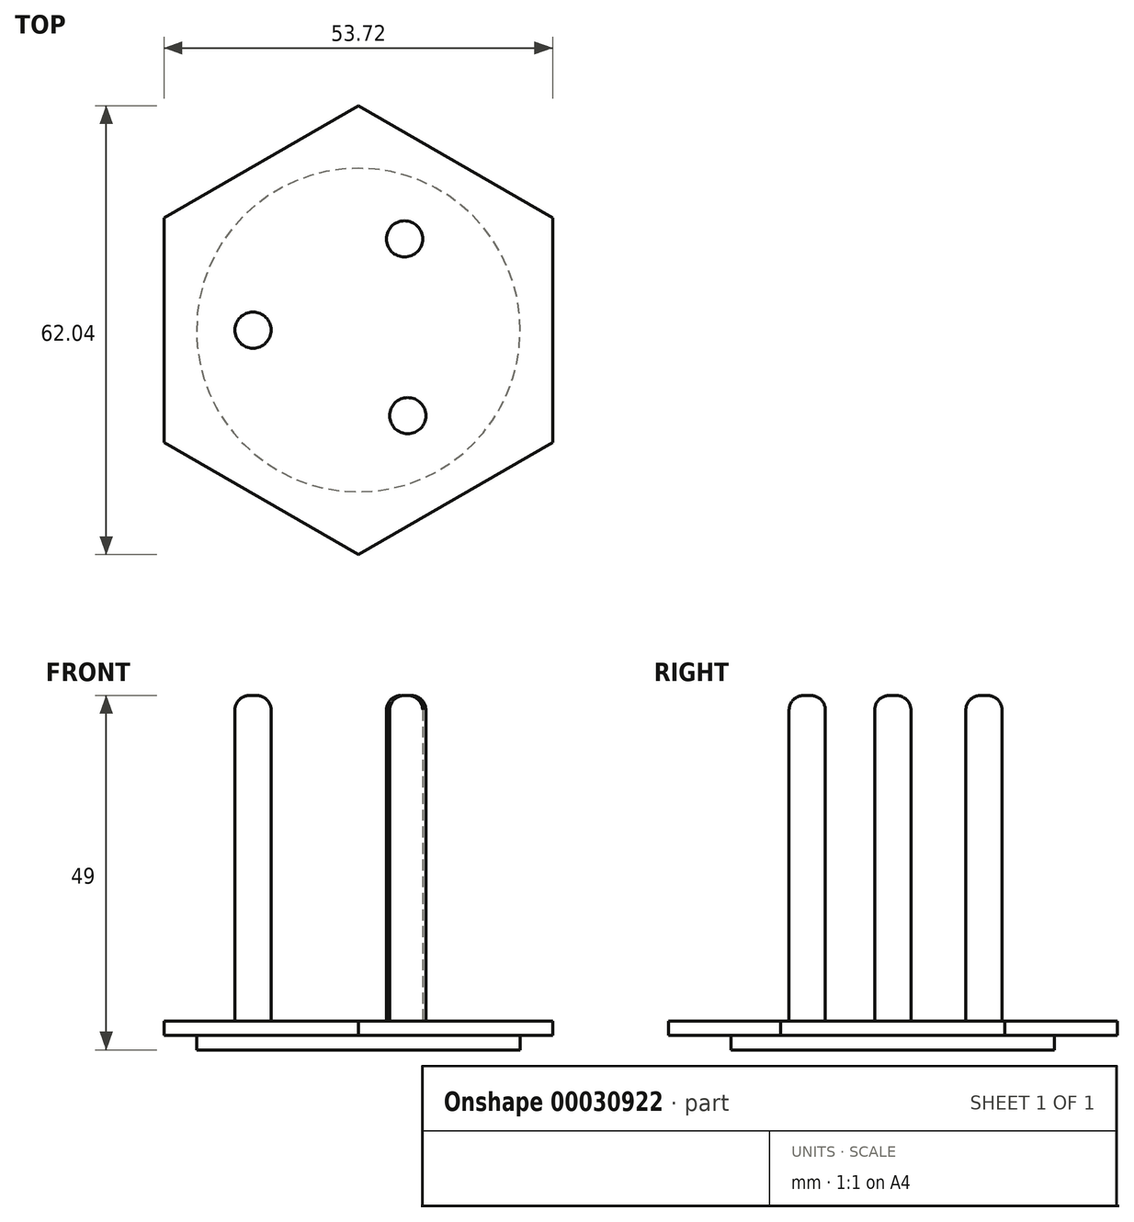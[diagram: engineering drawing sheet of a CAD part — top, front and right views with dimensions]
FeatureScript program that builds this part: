
annotation { "Feature Type Name" : "Feature", "Feature Type Description" : "" }
export const myFeature = defineFeature(function(context is Context, id is Id, definition is map)
    precondition{}
    {
        {
            var Q0;
            Q0=qCreatedBy(makeId("Top.planeOp"),FACE);
            var sketch = newSketch(context, id + "F0", { "sketchPlane" : qUnion([Q0])});
            skCircle(sketch, "E0.cCircle", {"center": v(0, 0) * mm, "radius": 26.86 * mm, "construction": true});
            skLineSegment(sketch, "E0.0", {"start": v(26.86, 15.51) * mm, "end": v(26.87, -15.51) * mm});
            skLineSegment(sketch, "E0.1", {"start": v(26.86, -15.51) * mm, "end": v(0, -31.02) * mm});
            skLineSegment(sketch, "E0.2", {"start": v(0, -31.02) * mm, "end": v(-26.86, -15.51) * mm});
            skLineSegment(sketch, "E0.3", {"start": v(-26.86, -15.51) * mm, "end": v(-26.87, 15.51) * mm});
            skLineSegment(sketch, "E0.4", {"start": v(-26.87, 15.51) * mm, "end": v(0, 31.02) * mm});
            skLineSegment(sketch, "E0.5", {"start": v(0, 31.02) * mm, "end": v(26.87, 15.51) * mm});
            skPoint(sketch, "E0.0.midPoint", {"position": v(26.86, 0) * mm});
            skCircle(sketch, "E1", {"center": v(0, 0) * mm, "radius": 22.36 * mm});
            skSolve(sketch);
        }
        {
            var Q0;
            Q0=makeQuery(id+"F0.imprint","IMPRINT",FACE,{"disambiguationData":[TD([[makeQuery(id+"F0.imprint","IMPRINT",EDGE,{"derivedFrom":sQuery(id+"F0.wireOp",EDGE,"E0.0")}),-1.0]])]});
            var Q1;
            Q1=makeQuery(id+"F0.imprint","IMPRINT",FACE,{"disambiguationData":[TD([[makeQuery(id+"F0.imprint","IMPRINT",EDGE,{"derivedFrom":sQuery(id+"F0.wireOp",EDGE,"E1")}),1.0]])]});
            extrude(context, id + "F1", {"entities" : qUnion([Q0, Q1]), "depth" : 2 * mm});
        }
        {
            var Q0;
            Q0=makeQuery(id+"F1.opExtrude","CAP_FACE",FACE,{"disambiguationData":[OSD([sQuery(id+"F0.wireOp",EDGE,"E0.0"),sQuery(id+"F0.wireOp",EDGE,"E0.1"),sQuery(id+"F0.wireOp",EDGE,"E0.2"),sQuery(id+"F0.wireOp",EDGE,"E0.3"),sQuery(id+"F0.wireOp",EDGE,"E0.4"),sQuery(id+"F0.wireOp",EDGE,"E0.5")])],"isStart":false});
            var sketch = newSketch(context, id + "F2", { "sketchPlane" : qUnion([Q0])});
            skCircle(sketch, "E2", {"center": v(-14.55, 0) * mm, "radius": 2.5 * mm});
            skCircle(sketch, "E3.1.0", {"center": v(6.83, -11.83) * mm, "radius": 2.5 * mm});
            skCircle(sketch, "E3.2.0", {"center": v(6.39, 12.6) * mm, "radius": 2.5 * mm});
            skPoint(sketch, "E3.center", {"position": v(-0.44, 0.26) * mm});
            skSolve(sketch);
        }
        {
            var Q0;
            Q0=makeQuery(id+"F2.imprint","IMPRINT",FACE,{"disambiguationData":[TD([[makeQuery(id+"F2.imprint","IMPRINT",EDGE,{"derivedFrom":sQuery(id+"F2.wireOp",EDGE,"E2")}),1.0]])]});
            var Q1;
            Q1=makeQuery(id+"F2.imprint","IMPRINT",FACE,{"disambiguationData":[TD([[makeQuery(id+"F2.imprint","IMPRINT",EDGE,{"derivedFrom":sQuery(id+"F2.wireOp",EDGE,"E3.2.0")}),1.0]])]});
            var Q2;
            Q2=makeQuery(id+"F2.imprint","IMPRINT",FACE,{"disambiguationData":[TD([[makeQuery(id+"F2.imprint","IMPRINT",EDGE,{"derivedFrom":sQuery(id+"F2.wireOp",EDGE,"E3.1.0")}),1.0]])]});
            var Q3;
            Q3=sQuery(id+"F2.wireOp",EDGE,"E2");
            extrude(context, id + "F3", {"entities" : qUnion([Q0, Q1, Q2]), "operationType" : NewBodyOperationType.ADD, "surfaceEntities" : qUnion([Q3]), "depth" : 45 * mm});
        }
        {
            var Q0;
            Q0=makeQuery(id+"F3.opExtrude","CAP_EDGE",EDGE,{"disambiguationData":[OSD([sQuery(id+"F2.wireOp",EDGE,"E2")])],"isStart":false});
            var Q1;
            Q1=makeQuery(id+"F3.opExtrude","CAP_EDGE",EDGE,{"disambiguationData":[OSD([sQuery(id+"F2.wireOp",EDGE,"E3.1.0")])],"isStart":false});
            var Q2;
            Q2=makeQuery(id+"F3.opExtrude","CAP_EDGE",EDGE,{"disambiguationData":[OSD([sQuery(id+"F2.wireOp",EDGE,"E3.2.0")])],"isStart":false});
            fillet(context, id + "F4", {"entities" : qUnion([Q0, Q1, Q2]), "radius" : 2 * mm, "tangentPropagation" : true, "allowEdgeOverflow" : false});
        }
        {
            var Q0;
            Q0=makeQuery(id+"F0.imprint","IMPRINT",FACE,{"disambiguationData":[TD([[makeQuery(id+"F0.imprint","IMPRINT",EDGE,{"derivedFrom":sQuery(id+"F0.wireOp",EDGE,"E1")}),1.0]])]});
            extrude(context, id + "F5", {"entities" : qUnion([Q0]), "operationType" : NewBodyOperationType.ADD, "oppositeDirection" : true, "depth" : 2 * mm});
        }
    });
